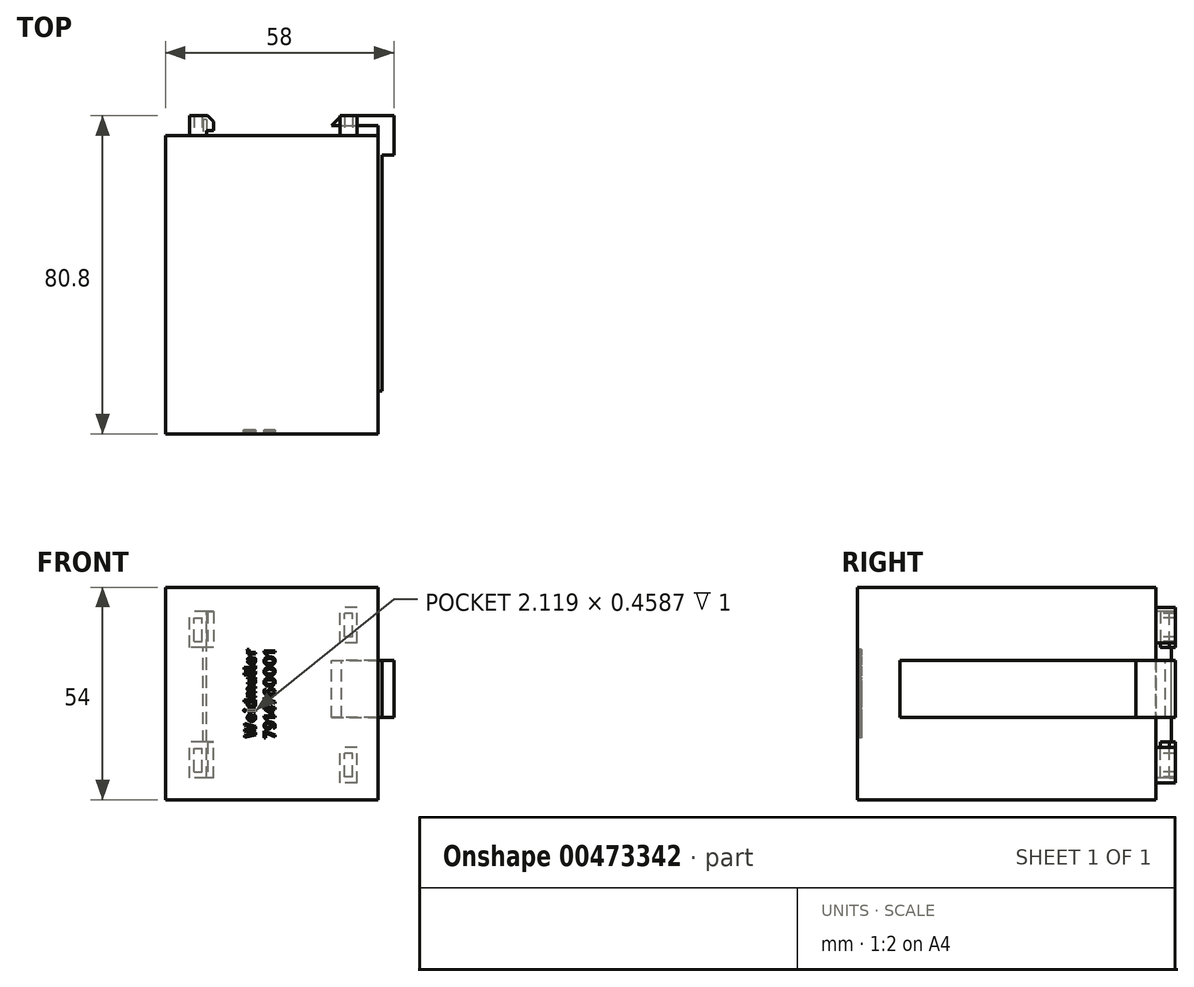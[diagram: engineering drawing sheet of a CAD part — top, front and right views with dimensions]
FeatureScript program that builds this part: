
annotation { "Feature Type Name" : "Feature", "Feature Type Description" : "" }
export const myFeature = defineFeature(function(context is Context, id is Id, definition is map)
    precondition{}
    {
        {
            var Q0;
            Q0=qCreatedBy(makeId("Top.planeOp"),FACE);
            var sketch = newSketch(context, id + "F0", { "sketchPlane" : qUnion([Q0])});
            skLineSegment(sketch, "E0.bottom", {"start": v(0, 0) * mm, "end": v(54, 0) * mm});
            skLineSegment(sketch, "E0.top", {"start": v(0, 74) * mm, "end": v(54, 74) * mm});
            skLineSegment(sketch, "E0.left", {"start": v(0, 0) * mm, "end": v(0, 74) * mm});
            skLineSegment(sketch, "E0.right", {"start": v(54, 0) * mm, "end": v(54, 74) * mm});
            skSolve(sketch);
        }
        {
            var Q0;
            Q0 = qSketchRegion(id + "F0", true);
            extrude(context, id + "F1", {"entities" : qUnion([Q0]), "depth" : 54 * mm});
        }
        {
            var Q0;
            Q0=makeQuery(id+"F1.opExtrude","SWEPT_FACE",FACE,{"disambiguationData":[OSD([sQuery(id+"F0.wireOp",EDGE,"E0.bottom")])]});
            var sketch = newSketch(context, id + "F2", { "sketchPlane" : qUnion([Q0])});
            skLineSegment(sketch, "E1.bottom", {"start": v(0, 0) * mm, "end": v(54, 0) * mm});
            skLineSegment(sketch, "E1.top", {"start": v(0, 54) * mm, "end": v(54, 54) * mm});
            skLineSegment(sketch, "E1.left", {"start": v(0, 0) * mm, "end": v(0, 54) * mm});
            skLineSegment(sketch, "E1.right", {"start": v(54, 0) * mm, "end": v(54, 54) * mm});
            skSolve(sketch);
        }
        {
            var Q0;
            Q0 = qSketchRegion(id + "F2", true);
            extrude(context, id + "F3", {"entities" : qUnion([Q0]), "operationType" : NewBodyOperationType.ADD, "depth" : 1.8 * mm});
        }
        {
            var Q0;
            Q0=makeQuery(id+"F3.boolean.opBoolean","MERGE",FACE,{"derivedFrom":[makeQuery(id+"F1.opExtrude","SWEPT_FACE",FACE,{"disambiguationData":[OSD([sQuery(id+"F0.wireOp",EDGE,"E0.right")])]}),makeQuery(id+"F3.opExtrude","SWEPT_FACE",FACE,{"disambiguationData":[OSD([sQuery(id+"F2.wireOp",EDGE,"E1.right")])]})]});
            var sketch = newSketch(context, id + "F4", { "sketchPlane" : qUnion([Q0])});
            skLineSegment(sketch, "E2.bottom", {"start": v(9, 35.37) * mm, "end": v(79, 35.37) * mm});
            skLineSegment(sketch, "E2.top", {"start": v(9, 20.87) * mm, "end": v(79, 20.87) * mm});
            skLineSegment(sketch, "E2.left", {"start": v(9, 35.37) * mm, "end": v(9, 20.87) * mm});
            skLineSegment(sketch, "E2.right", {"start": v(79, 35.37) * mm, "end": v(79, 20.87) * mm});
            skSolve(sketch);
        }
        {
            var Q0;
            Q0 = qSketchRegion(id + "F4", true);
            extrude(context, id + "F5", {"entities" : qUnion([Q0]), "operationType" : NewBodyOperationType.ADD, "depth" : 1 * mm});
        }
        {
            var Q0;
            Q0=makeQuery(id+"F5.opExtrude","CAP_FACE",FACE,{"disambiguationData":[OSD([sQuery(id+"F4.wireOp",EDGE,"E2.bottom"),sQuery(id+"F4.wireOp",EDGE,"E2.top"),sQuery(id+"F4.wireOp",EDGE,"E2.left"),sQuery(id+"F4.wireOp",EDGE,"E2.right")])],"isStart":false});
            var sketch = newSketch(context, id + "F6", { "sketchPlane" : qUnion([Q0])});
            skLineSegment(sketch, "E3.bottom", {"start": v(79, 35.37) * mm, "end": v(69, 35.37) * mm});
            skLineSegment(sketch, "E3.top", {"start": v(79, 20.87) * mm, "end": v(69, 20.87) * mm});
            skLineSegment(sketch, "E3.left", {"start": v(79, 35.37) * mm, "end": v(79, 20.87) * mm});
            skLineSegment(sketch, "E3.right", {"start": v(69, 35.37) * mm, "end": v(69, 20.87) * mm});
            skSolve(sketch);
        }
        {
            var Q0;
            Q0 = qSketchRegion(id + "F6", true);
            extrude(context, id + "F7", {"entities" : qUnion([Q0]), "operationType" : NewBodyOperationType.ADD, "depth" : 3 * mm});
        }
        {
            var Q0;
            Q0=makeQuery(id+"F1.opExtrude","SWEPT_FACE",FACE,{"disambiguationData":[OSD([sQuery(id+"F0.wireOp",EDGE,"E0.top")])]});
            var sketch = newSketch(context, id + "F8", { "sketchPlane" : qUnion([Q0])});
            skLineSegment(sketch, "E4.bottom", {"start": v(-48.6, 4.24) * mm, "end": v(-44.3, 4.24) * mm});
            skLineSegment(sketch, "E4.top", {"start": v(-48.6, 13.34) * mm, "end": v(-44.3, 13.34) * mm});
            skLineSegment(sketch, "E4.left", {"start": v(-48.6, 4.24) * mm, "end": v(-48.6, 13.34) * mm});
            skLineSegment(sketch, "E4.right", {"start": v(-44.3, 4.24) * mm, "end": v(-44.3, 13.34) * mm});
            skLineSegment(sketch, "E5.bottom", {"start": v(-48.6, 39.8) * mm, "end": v(-44.3, 39.8) * mm});
            skLineSegment(sketch, "E5.top", {"start": v(-48.6, 48.9) * mm, "end": v(-44.3, 48.9) * mm});
            skLineSegment(sketch, "E5.left", {"start": v(-48.6, 39.8) * mm, "end": v(-48.6, 48.9) * mm});
            skLineSegment(sketch, "E5.right", {"start": v(-44.3, 39.8) * mm, "end": v(-44.3, 48.9) * mm});
            skLineSegment(sketch, "E6.bottom", {"start": v(-10.42, 5.54) * mm, "end": v(-6.12, 5.54) * mm});
            skLineSegment(sketch, "E6.top", {"start": v(-10.42, 14.64) * mm, "end": v(-6.12, 14.64) * mm});
            skLineSegment(sketch, "E6.left", {"start": v(-10.42, 5.54) * mm, "end": v(-10.42, 14.64) * mm});
            skLineSegment(sketch, "E6.right", {"start": v(-6.12, 5.54) * mm, "end": v(-6.12, 14.64) * mm});
            skLineSegment(sketch, "E7.bottom", {"start": v(-10.42, 38.7) * mm, "end": v(-6.12, 38.7) * mm});
            skLineSegment(sketch, "E7.top", {"start": v(-10.42, 47.8) * mm, "end": v(-6.12, 47.8) * mm});
            skLineSegment(sketch, "E7.left", {"start": v(-10.42, 38.7) * mm, "end": v(-10.42, 47.8) * mm});
            skLineSegment(sketch, "E7.right", {"start": v(-6.12, 38.7) * mm, "end": v(-6.12, 47.8) * mm});
            skLineSegment(sketch, "E8.bottom", {"start": v(-47.44, 5.8) * mm, "end": v(-45.44, 5.8) * mm});
            skLineSegment(sketch, "E8.top", {"start": v(-47.44, 11.8) * mm, "end": v(-45.44, 11.8) * mm});
            skLineSegment(sketch, "E8.left", {"start": v(-47.44, 5.8) * mm, "end": v(-47.44, 11.8) * mm});
            skLineSegment(sketch, "E8.right", {"start": v(-45.44, 5.8) * mm, "end": v(-45.44, 11.8) * mm});
            skLineSegment(sketch, "E9.bottom", {"start": v(-47.44, 41.35) * mm, "end": v(-45.44, 41.35) * mm});
            skLineSegment(sketch, "E9.top", {"start": v(-47.44, 47.35) * mm, "end": v(-45.44, 47.35) * mm});
            skLineSegment(sketch, "E9.left", {"start": v(-47.44, 41.35) * mm, "end": v(-47.44, 47.35) * mm});
            skLineSegment(sketch, "E9.right", {"start": v(-45.44, 41.35) * mm, "end": v(-45.44, 47.35) * mm});
            skLineSegment(sketch, "E10.bottom", {"start": v(-7.27, 40.24) * mm, "end": v(-9.27, 40.24) * mm});
            skLineSegment(sketch, "E10.top", {"start": v(-7.27, 46.24) * mm, "end": v(-9.27, 46.24) * mm});
            skLineSegment(sketch, "E10.left", {"start": v(-7.27, 40.24) * mm, "end": v(-7.27, 46.24) * mm});
            skLineSegment(sketch, "E10.right", {"start": v(-9.27, 40.24) * mm, "end": v(-9.27, 46.24) * mm});
            skLineSegment(sketch, "E11.bottom", {"start": v(-7.27, 7.1) * mm, "end": v(-9.27, 7.1) * mm});
            skLineSegment(sketch, "E11.top", {"start": v(-7.27, 13.1) * mm, "end": v(-9.27, 13.1) * mm});
            skLineSegment(sketch, "E11.left", {"start": v(-7.27, 7.1) * mm, "end": v(-7.27, 13.1) * mm});
            skLineSegment(sketch, "E11.right", {"start": v(-9.27, 7.1) * mm, "end": v(-9.27, 13.1) * mm});
            skSolve(sketch);
        }
        {
            var Q0;
            Q0 = qSketchRegion(id + "F8", true);
            extrude(context, id + "F9", {"entities" : qUnion([Q0]), "operationType" : NewBodyOperationType.ADD, "depth" : 5 * mm});
        }
        {
            var Q0;
            {var subQ2=sQuery(id+"F0.wireOp",EDGE,"E0.left");var subQ3=sQuery(id+"F0.wireOp",EDGE,"E0.top");Q0=makeQuery(id+"F9.boolean.opBoolean","SPLIT",FACE,{"disambiguationData":[TD([makeQuery(id+"F1.opExtrude","SWEPT_FACE",FACE,{"disambiguationData":[OSD([subQ2])]})])],"derivedFrom":makeQuery(id+"F1.opExtrude","SWEPT_FACE",FACE,{"disambiguationData":[OSD([subQ3])]})});}
            var sketch = newSketch(context, id + "F10", { "sketchPlane" : qUnion([Q0])});
            skLineSegment(sketch, "E12.bottom", {"start": v(-10.42, 14.64) * mm, "end": v(-9.48, 14.64) * mm});
            skLineSegment(sketch, "E12.top", {"start": v(-10.42, 38.7) * mm, "end": v(-9.48, 38.7) * mm});
            skLineSegment(sketch, "E12.left", {"start": v(-10.42, 14.64) * mm, "end": v(-10.42, 38.7) * mm});
            skLineSegment(sketch, "E12.right", {"start": v(-9.48, 14.64) * mm, "end": v(-9.48, 38.7) * mm});
            skSolve(sketch);
        }
        {
            var Q0;
            Q0 = qSketchRegion(id + "F10", true);
            extrude(context, id + "F11", {"entities" : qUnion([Q0]), "operationType" : NewBodyOperationType.ADD, "depth" : 4 * mm});
        }
        {
            var Q0;
            Q0=makeQuery(id+"F11.boolean.opBoolean","MERGE",FACE,{"derivedFrom":[makeQuery(id+"F9.opExtrude","SWEPT_FACE",FACE,{"disambiguationData":[OSD([sQuery(id+"F8.wireOp",EDGE,"E6.left")])]}),makeQuery(id+"F9.opExtrude","SWEPT_FACE",FACE,{"disambiguationData":[OSD([sQuery(id+"F8.wireOp",EDGE,"E7.left")])]}),makeQuery(id+"F11.opExtrude","SWEPT_FACE",FACE,{"disambiguationData":[OSD([sQuery(id+"F10.wireOp",EDGE,"E12.left")])]})]});
            var sketch = newSketch(context, id + "F12", { "sketchPlane" : qUnion([Q0])});
            skLineSegment(sketch, "E13.bottom", {"start": v(79, 5.54) * mm, "end": v(75.2, 5.54) * mm});
            skLineSegment(sketch, "E13.top", {"start": v(79, 14.64) * mm, "end": v(75.2, 14.64) * mm});
            skLineSegment(sketch, "E13.left", {"start": v(79, 5.54) * mm, "end": v(79, 14.64) * mm});
            skLineSegment(sketch, "E13.right", {"start": v(75.2, 5.54) * mm, "end": v(75.2, 14.64) * mm});
            skLineSegment(sketch, "E14.bottom", {"start": v(79, 47.8) * mm, "end": v(75.2, 47.8) * mm});
            skLineSegment(sketch, "E14.top", {"start": v(79, 38.7) * mm, "end": v(75.2, 38.7) * mm});
            skLineSegment(sketch, "E14.left", {"start": v(79, 47.8) * mm, "end": v(79, 38.7) * mm});
            skLineSegment(sketch, "E14.right", {"start": v(75.2, 47.8) * mm, "end": v(75.2, 38.7) * mm});
            skSolve(sketch);
        }
        {
            var Q0;
            Q0 = qSketchRegion(id + "F12", true);
            extrude(context, id + "F13", {"entities" : qUnion([Q0]), "operationType" : NewBodyOperationType.ADD, "depth" : 1.8 * mm});
        }
        {
            var Q0;
            Q0=makeQuery(id+"F13.opExtrude","CAP_EDGE",EDGE,{"disambiguationData":[OSD([sQuery(id+"F12.wireOp",EDGE,"E14.left")])],"isStart":false});
            var Q1;
            Q1=makeQuery(id+"F13.opExtrude","CAP_EDGE",EDGE,{"disambiguationData":[OSD([sQuery(id+"F12.wireOp",EDGE,"E13.left")])],"isStart":false});
            chamfer(context, id + "F14", {"entities" : qUnion([Q0, Q1]), "width" : 1.5 * mm, "tangentPropagation" : true});
        }
        {
            var Q0;
            Q0=makeQuery(id+"F5.opExtrude","CAP_FACE",FACE,{"disambiguationData":[OSD([sQuery(id+"F4.wireOp",EDGE,"E2.bottom"),sQuery(id+"F4.wireOp",EDGE,"E2.top"),sQuery(id+"F4.wireOp",EDGE,"E2.left"),sQuery(id+"F4.wireOp",EDGE,"E2.right")])],"isStart":true});
            var sketch = newSketch(context, id + "F15", { "sketchPlane" : qUnion([Q0])});
            skLineSegment(sketch, "E15.bottom", {"start": v(-79, 20.87) * mm, "end": v(-76.5, 20.87) * mm});
            skLineSegment(sketch, "E15.top", {"start": v(-79, 35.37) * mm, "end": v(-76.5, 35.37) * mm});
            skLineSegment(sketch, "E15.left", {"start": v(-79, 20.87) * mm, "end": v(-79, 35.37) * mm});
            skLineSegment(sketch, "E15.right", {"start": v(-76.5, 20.87) * mm, "end": v(-76.5, 35.37) * mm});
            skSolve(sketch);
        }
        {
            var Q0;
            Q0 = qSketchRegion(id + "F15", true);
            extrude(context, id + "F16", {"entities" : qUnion([Q0]), "operationType" : NewBodyOperationType.ADD, "depth" : 11.8 * mm});
        }
        {
            var Q0;
            Q0=makeQuery(id+"F16.opExtrude","CAP_EDGE",EDGE,{"disambiguationData":[OSD([sQuery(id+"F15.wireOp",EDGE,"E15.left")])],"isStart":false});
            chamfer(context, id + "F17", {"entities" : qUnion([Q0]), "width" : 2.5 * mm, "tangentPropagation" : true});
        }
        {
            var Q0;
            Q0=makeQuery(id+"F3.opExtrude","CAP_FACE",FACE,{"disambiguationData":[OSD([sQuery(id+"F2.wireOp",EDGE,"E1.bottom"),sQuery(id+"F2.wireOp",EDGE,"E1.top"),sQuery(id+"F2.wireOp",EDGE,"E1.left"),sQuery(id+"F2.wireOp",EDGE,"E1.right")])],"isStart":false});
            var sketch = newSketch(context, id + "F18", { "sketchPlane" : qUnion([Q0])});
            skText(sketch, "E16", { "text": "Weidmuller\n7914760001", "fontName": "AllertaStencil-Regular.ttf"});
            const initialGuessF18  = {"E16": [0.0229, 0.01553, 0, 1, 0.00277]};
            skSetInitialGuess(sketch, initialGuessF18);
            skSolve(sketch);
        }
        {
            var Q0;
            Q0 = qSketchRegion(id + "F18", true);
            extrude(context, id + "F19", {"entities" : qUnion([Q0]), "operationType" : NewBodyOperationType.REMOVE, "oppositeDirection" : true, "depth" : 1 * mm});
        }
    });
